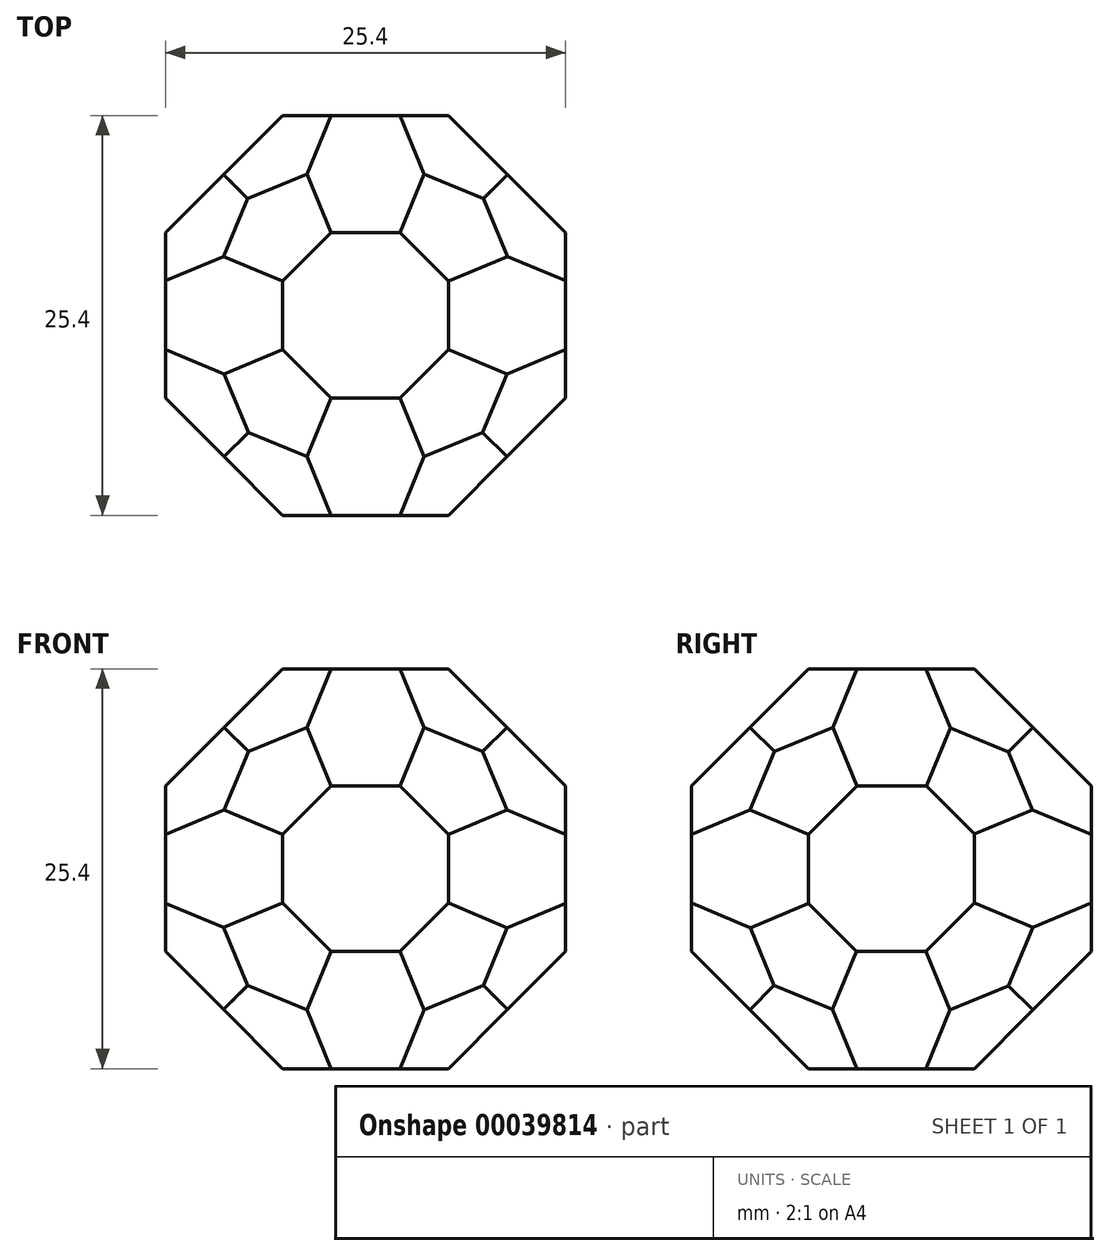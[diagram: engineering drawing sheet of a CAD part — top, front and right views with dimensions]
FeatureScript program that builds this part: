
annotation { "Feature Type Name" : "Feature", "Feature Type Description" : "" }
export const myFeature = defineFeature(function(context is Context, id is Id, definition is map)
    precondition{}
    {
        {
            var Q0;
            Q0=qCreatedBy(makeId("Right.planeOp"),FACE);
            var sketch = newSketch(context, id + "F0", { "sketchPlane" : qUnion([Q0])});
            skCircle(sketch, "E0.cCircle", {"center": v(0, 0) * mm, "radius": 12.7 * mm, "construction": true});
            skLineSegment(sketch, "E0.0", {"start": v(-5.26, 12.7) * mm, "end": v(5.26, 12.7) * mm});
            skLineSegment(sketch, "E0.1", {"start": v(5.26, 12.7) * mm, "end": v(12.7, 5.26) * mm});
            skLineSegment(sketch, "E0.2", {"start": v(12.7, 5.26) * mm, "end": v(12.7, -5.26) * mm});
            skLineSegment(sketch, "E0.3", {"start": v(12.7, -5.26) * mm, "end": v(5.26, -12.7) * mm});
            skLineSegment(sketch, "E0.4", {"start": v(5.26, -12.7) * mm, "end": v(-5.26, -12.7) * mm});
            skLineSegment(sketch, "E0.5", {"start": v(-5.26, -12.7) * mm, "end": v(-12.7, -5.26) * mm});
            skLineSegment(sketch, "E0.6", {"start": v(-12.7, -5.26) * mm, "end": v(-12.7, 5.26) * mm});
            skLineSegment(sketch, "E0.7", {"start": v(-12.7, 5.26) * mm, "end": v(-5.26, 12.7) * mm});
            skPoint(sketch, "E0.0.midPoint", {"position": v(0, 12.7) * mm});
            skSolve(sketch);
        }
        {
            var Q0;
            Q0 = qSketchRegion(id + "F0", true);
            extrude(context, id + "F1", {"entities" : qUnion([Q0]), "endBound" : BoundingType.SYMMETRIC, "depth" : 25.4 * mm});
        }
        {
            var Q0;
            Q0=qCreatedBy(makeId("Top.planeOp"),FACE);
            var sketch = newSketch(context, id + "F2", { "sketchPlane" : qUnion([Q0])});
            skArc(sketch, "E1.cCircle", {"start": v(-8.98, 8.98) * mm, "mid": v(4.86, -11.73) * mm, "end": v(0, 12.7) * mm, "construction": true});
            skLineSegment(sketch, "E1.1", {"start": v(5.26, 12.7) * mm, "end": v(12.7, 5.26) * mm});
            skLineSegment(sketch, "E1.3", {"start": v(12.7, -5.26) * mm, "end": v(5.26, -12.7) * mm});
            skLineSegment(sketch, "E1.5", {"start": v(-5.26, -12.7) * mm, "end": v(-12.7, -5.26) * mm});
            skLineSegment(sketch, "E1.7", {"start": v(-12.7, 5.26) * mm, "end": v(-5.26, 12.7) * mm});
            skPoint(sketch, "E1.0.midPoint", {"position": v(0, 12.7) * mm});
            skLineSegment(sketch, "E2", {"start": v(-12.7, 5.26) * mm, "end": v(-12.7, 13.88) * mm});
            skLineSegment(sketch, "E3", {"start": v(-12.7, 13.88) * mm, "end": v(-12.7, 12.75) * mm});
            skLineSegment(sketch, "E4", {"start": v(-5.26, 12.7) * mm, "end": v(-13.31, 12.75) * mm});
            skLineSegment(sketch, "E5", {"start": v(-13.31, 12.75) * mm, "end": v(-12.7, 12.75) * mm});
            skLineSegment(sketch, "E6", {"start": v(16.73, 12.75) * mm, "end": v(12.98, 12.75) * mm});
            skLineSegment(sketch, "E7", {"start": v(12.7, 5.26) * mm, "end": v(12.7, 12.75) * mm});
            skLineSegment(sketch, "E8", {"start": v(12.7, 12.75) * mm, "end": v(12.7, 5.26) * mm});
            skLineSegment(sketch, "E9", {"start": v(12.7, 5.26) * mm, "end": v(5.26, 12.7) * mm});
            skLineSegment(sketch, "E10.0", {"start": v(12.7, -12.7) * mm, "end": v(12.7, -5.26) * mm});
            skLineSegment(sketch, "E11.0", {"start": v(12.7, -12.7) * mm, "end": v(-12.7, -12.7) * mm});
            skLineSegment(sketch, "E12.0", {"start": v(-12.7, -12.7) * mm, "end": v(-12.7, -5.26) * mm});
            skLineSegment(sketch, "E13.trimOffspring", {"start": v(12.7, 12.75) * mm, "end": v(16.73, 12.75) * mm});
            skLineSegment(sketch, "E14", {"start": v(5.26, 12.7) * mm, "end": v(14.71, 12.75) * mm});
            skSolve(sketch);
        }
        {
            var Q0;
            Q0 = qSketchRegion(id + "F2", true);
            extrude(context, id + "F3", {"entities" : qUnion([Q0]), "operationType" : NewBodyOperationType.REMOVE, "endBound" : BoundingType.SYMMETRIC, "oppositeDirection" : true, "depth" : 25.4 * mm});
        }
        {
            var Q0;
            Q0=makeQuery(id+"F1.opExtrude","SWEPT_FACE",FACE,{"disambiguationData":[OSD([sQuery(id+"F0.wireOp",EDGE,"E0.2")])]});
            var sketch = newSketch(context, id + "F4", { "sketchPlane" : qUnion([Q0])});
            skArc(sketch, "E15.cCircle", {"start": v(-8.98, 8.98) * mm, "mid": v(-8.98, -8.98) * mm, "end": v(8.98, -8.98) * mm, "construction": true});
            skLineSegment(sketch, "E15.1", {"start": v(5.26, 12.7) * mm, "end": v(12.7, 5.26) * mm});
            skLineSegment(sketch, "E15.3", {"start": v(12.7, -5.26) * mm, "end": v(5.26, -12.7) * mm});
            skLineSegment(sketch, "E15.4", {"start": v(5.26, -12.7) * mm, "end": v(-5.26, -12.7) * mm});
            skLineSegment(sketch, "E15.5", {"start": v(-5.26, -12.7) * mm, "end": v(-12.7, -5.26) * mm});
            skLineSegment(sketch, "E15.6", {"start": v(-12.7, -5.26) * mm, "end": v(-12.7, 0) * mm});
            skLineSegment(sketch, "E15.7", {"start": v(-12.7, 5.26) * mm, "end": v(-5.26, 12.7) * mm});
            skPoint(sketch, "E15.0.midPoint", {"position": v(0, 12.7) * mm});
            skPoint(sketch, "E16.0.start.orphan", {"position": v(-12.7, 12.7) * mm});
            skPoint(sketch, "E17.0.end.orphan", {"position": v(12.7, 12.7) * mm});
            skPoint(sketch, "E18.0.end.orphan", {"position": v(12.7, -12.7) * mm});
            skPoint(sketch, "E18.0.start.orphan", {"position": v(-12.7, -12.7) * mm});
            skLineSegment(sketch, "E19.0", {"start": v(-12.7, -12.7) * mm, "end": v(-12.7, -5.26) * mm});
            skLineSegment(sketch, "E20.0", {"start": v(-12.7, 12.7) * mm, "end": v(-5.26, 12.7) * mm});
            skLineSegment(sketch, "E21.0", {"start": v(12.7, -12.7) * mm, "end": v(12.7, -5.26) * mm});
            skLineSegment(sketch, "E22.0", {"start": v(-12.7, -12.7) * mm, "end": v(0, -12.7) * mm});
            skLineSegment(sketch, "E23.trimOffspring", {"start": v(-12.7, 5.26) * mm, "end": v(-12.7, 12.7) * mm});
            skLineSegment(sketch, "E24.trimOffspring", {"start": v(5.26, 12.7) * mm, "end": v(12.7, 12.7) * mm});
            skLineSegment(sketch, "E25.trimOffspring", {"start": v(12.7, 0) * mm, "end": v(12.7, 12.7) * mm});
            skLineSegment(sketch, "E26.trimOffspring", {"start": v(5.26, -12.7) * mm, "end": v(12.7, -12.7) * mm});
            skSolve(sketch);
        }
        {
            var Q0;
            Q0 = qSketchRegion(id + "F4", true);
            extrude(context, id + "F5", {"entities" : qUnion([Q0]), "operationType" : NewBodyOperationType.REMOVE, "oppositeDirection" : true, "depth" : 25.4 * mm});
        }
        {
            var Q0;
            Q0=makeQuery(id+"F1.opExtrude","SWEPT_FACE",FACE,{"disambiguationData":[OSD([sQuery(id+"F0.wireOp",EDGE,"E0.7")])]});
            var sketch = newSketch(context, id + "F6", { "sketchPlane" : qUnion([Q0])});
            skCircle(sketch, "E27.cCircle", {"center": v(0, 0) * mm, "radius": 12.72 * mm, "construction": true});
            skLineSegment(sketch, "E27.0", {"start": v(-12.72, -5.27) * mm, "end": v(-12.72, 5.27) * mm});
            skLineSegment(sketch, "E27.1", {"start": v(-12.72, 5.27) * mm, "end": v(-5.27, 12.72) * mm});
            skLineSegment(sketch, "E27.2", {"start": v(-5.27, 12.72) * mm, "end": v(5.27, 12.72) * mm});
            skLineSegment(sketch, "E27.3", {"start": v(5.27, 12.72) * mm, "end": v(12.72, 5.27) * mm});
            skLineSegment(sketch, "E27.4", {"start": v(12.72, 0) * mm, "end": v(12.72, -5.27) * mm});
            skLineSegment(sketch, "E27.5", {"start": v(12.72, -5.27) * mm, "end": v(5.27, -12.72) * mm});
            skLineSegment(sketch, "E27.6", {"start": v(5.27, -12.72) * mm, "end": v(0, -12.72) * mm});
            skLineSegment(sketch, "E27.7", {"start": v(-5.27, -12.72) * mm, "end": v(-12.72, -5.27) * mm});
            skPoint(sketch, "E27.0.midPoint", {"position": v(-12.72, 0) * mm});
            skLineSegment(sketch, "E28", {"start": v(-5.27, -12.72) * mm, "end": v(-14.84, -12.72) * mm});
            skLineSegment(sketch, "E29", {"start": v(-14.84, -12.72) * mm, "end": v(-14.84, -4.68) * mm});
            skLineSegment(sketch, "E30", {"start": v(-14.84, -4.68) * mm, "end": v(-12.72, -5.27) * mm});
            skLineSegment(sketch, "E31", {"start": v(-12.72, 5.27) * mm, "end": v(-16.15, 5.27) * mm});
            skLineSegment(sketch, "E32", {"start": v(-16.15, 5.27) * mm, "end": v(-10.66, 15.36) * mm});
            skLineSegment(sketch, "E33", {"start": v(-10.66, 15.36) * mm, "end": v(-5.27, 12.72) * mm});
            skLineSegment(sketch, "E34", {"start": v(5.27, 12.72) * mm, "end": v(11.88, 14.74) * mm});
            skLineSegment(sketch, "E35", {"start": v(11.88, 14.74) * mm, "end": v(15.12, 7.12) * mm});
            skLineSegment(sketch, "E36", {"start": v(15.12, 7.12) * mm, "end": v(12.72, 5.27) * mm});
            skLineSegment(sketch, "E37", {"start": v(5.27, -12.72) * mm, "end": v(11.63, -17.16) * mm});
            skLineSegment(sketch, "E38", {"start": v(11.63, -17.16) * mm, "end": v(17.18, -6.74) * mm});
            skLineSegment(sketch, "E39", {"start": v(17.18, -6.74) * mm, "end": v(12.72, -5.27) * mm});
            skSolve(sketch);
        }
        {
            var Q0;
            Q0 = qSketchRegion(id + "F6", true);
            extrude(context, id + "F7", {"entities" : qUnion([Q0]), "operationType" : NewBodyOperationType.REMOVE, "oppositeDirection" : true, "depth" : 25.4 * mm});
        }
        {
            var Q0;
            Q0=makeQuery(id+"F1.opExtrude","SWEPT_FACE",FACE,{"disambiguationData":[OSD([sQuery(id+"F0.wireOp",EDGE,"E0.5")])]});
            var sketch = newSketch(context, id + "F8", { "sketchPlane" : qUnion([Q0])});
            skCircle(sketch, "E40.cCircle", {"center": v(0, 0) * mm, "radius": 12.7 * mm, "construction": true});
            skLineSegment(sketch, "E40.0", {"start": v(12.7, 5.26) * mm, "end": v(12.7, -5.26) * mm});
            skLineSegment(sketch, "E40.1", {"start": v(12.7, -5.26) * mm, "end": v(5.26, -12.7) * mm});
            skLineSegment(sketch, "E40.2", {"start": v(5.26, -12.7) * mm, "end": v(-5.26, -12.7) * mm});
            skLineSegment(sketch, "E40.3", {"start": v(-5.26, -12.7) * mm, "end": v(-12.7, -5.26) * mm});
            skLineSegment(sketch, "E40.4", {"start": v(-12.7, -5.26) * mm, "end": v(-12.7, 5.26) * mm});
            skLineSegment(sketch, "E40.5", {"start": v(-12.7, 5.26) * mm, "end": v(-5.26, 12.7) * mm});
            skLineSegment(sketch, "E40.6", {"start": v(-5.26, 12.7) * mm, "end": v(5.26, 12.7) * mm});
            skLineSegment(sketch, "E40.7", {"start": v(5.26, 12.7) * mm, "end": v(12.7, 5.26) * mm});
            skPoint(sketch, "E40.0.midPoint", {"position": v(12.7, 0) * mm});
            skLineSegment(sketch, "E41", {"start": v(12.7, 5.26) * mm, "end": v(15.02, 5.97) * mm});
            skLineSegment(sketch, "E42", {"start": v(15.02, 5.97) * mm, "end": v(8.38, 16.37) * mm});
            skLineSegment(sketch, "E43", {"start": v(8.38, 16.37) * mm, "end": v(5.26, 12.7) * mm});
            skLineSegment(sketch, "E44", {"start": v(-5.26, 12.7) * mm, "end": v(-10.87, 17.6) * mm});
            skLineSegment(sketch, "E45", {"start": v(-10.87, 17.6) * mm, "end": v(-15.85, 5.64) * mm});
            skLineSegment(sketch, "E46", {"start": v(-15.85, 5.64) * mm, "end": v(-12.7, 5.26) * mm});
            skLineSegment(sketch, "E47", {"start": v(-12.7, -5.26) * mm, "end": v(-15.77, -8.33) * mm});
            skLineSegment(sketch, "E48", {"start": v(-15.77, -8.33) * mm, "end": v(-6.61, -16.65) * mm});
            skLineSegment(sketch, "E49", {"start": v(-6.61, -16.65) * mm, "end": v(-5.26, -12.7) * mm});
            skLineSegment(sketch, "E50", {"start": v(12.7, -5.26) * mm, "end": v(16.3, -8.85) * mm});
            skLineSegment(sketch, "E51", {"start": v(16.3, -8.85) * mm, "end": v(9.21, -16.87) * mm});
            skLineSegment(sketch, "E52", {"start": v(9.21, -16.87) * mm, "end": v(5.26, -12.7) * mm});
            skSolve(sketch);
        }
        {
            var Q0;
            Q0=makeQuery(id+"F8.imprint","IMPRINT",FACE,{"disambiguationData":[TD([[makeQuery(id+"F8.imprint","IMPRINT",EDGE,{"derivedFrom":sQuery(id+"F8.wireOp",EDGE,"E40.1")}),1.0]])]});
            var Q1;
            Q1=makeQuery(id+"F8.imprint","IMPRINT",FACE,{"disambiguationData":[TD([[makeQuery(id+"F8.imprint","IMPRINT",EDGE,{"derivedFrom":sQuery(id+"F8.wireOp",EDGE,"E40.3")}),1.0]])]});
            var Q2;
            Q2=makeQuery(id+"F8.imprint","IMPRINT",FACE,{"disambiguationData":[TD([[makeQuery(id+"F8.imprint","IMPRINT",EDGE,{"derivedFrom":sQuery(id+"F8.wireOp",EDGE,"E40.5")}),1.0]])]});
            var Q3;
            Q3=makeQuery(id+"F8.imprint","IMPRINT",FACE,{"disambiguationData":[TD([[makeQuery(id+"F8.imprint","IMPRINT",EDGE,{"derivedFrom":sQuery(id+"F8.wireOp",EDGE,"E40.7")}),1.0]])]});
            extrude(context, id + "F9", {"entities" : qUnion([Q0, Q1, Q2, Q3]), "operationType" : NewBodyOperationType.REMOVE, "oppositeDirection" : true, "depth" : 25.4 * mm});
        }
        {
            var Q0;
            Q0=makeQuery(id+"F5.boolean.opBoolean","COPY",FACE,{"derivedFrom":makeQuery(id+"F5.opExtrude","SWEPT_FACE",FACE,{"disambiguationData":[OSD([sQuery(id+"F4.wireOp",EDGE,"E15.1")])]})});
            var sketch = newSketch(context, id + "F10", { "sketchPlane" : qUnion([Q0])});
            skCircle(sketch, "E53.cCircle", {"center": v(0, 0) * mm, "radius": 12.7 * mm, "construction": true});
            skLineSegment(sketch, "E53.0", {"start": v(0, 12.7) * mm, "end": v(5.26, 12.7) * mm});
            skLineSegment(sketch, "E53.1", {"start": v(5.26, 12.7) * mm, "end": v(12.7, 5.26) * mm});
            skLineSegment(sketch, "E53.2", {"start": v(12.7, 5.26) * mm, "end": v(12.7, -5.26) * mm});
            skLineSegment(sketch, "E53.3", {"start": v(12.7, -5.26) * mm, "end": v(5.26, -12.7) * mm});
            skLineSegment(sketch, "E53.4", {"start": v(5.26, -12.7) * mm, "end": v(-5.26, -12.7) * mm});
            skLineSegment(sketch, "E53.5", {"start": v(-5.26, -12.7) * mm, "end": v(-12.7, -5.26) * mm});
            skLineSegment(sketch, "E53.6", {"start": v(-12.7, -5.26) * mm, "end": v(-12.7, 5.26) * mm});
            skLineSegment(sketch, "E53.7", {"start": v(-12.7, 5.26) * mm, "end": v(-5.26, 12.7) * mm});
            skPoint(sketch, "E53.0.midPoint", {"position": v(0, 12.7) * mm});
            skLineSegment(sketch, "E54", {"start": v(-12.7, 5.26) * mm, "end": v(-12.7, 11.55) * mm});
            skLineSegment(sketch, "E55", {"start": v(-12.7, 11.55) * mm, "end": v(-5.26, 12.7) * mm});
            skLineSegment(sketch, "E56", {"start": v(5.26, 12.7) * mm, "end": v(15.02, 11.13) * mm});
            skLineSegment(sketch, "E57", {"start": v(15.02, 11.13) * mm, "end": v(12.7, 5.26) * mm});
            skLineSegment(sketch, "E58", {"start": v(12.7, -5.26) * mm, "end": v(14.34, -10.45) * mm});
            skLineSegment(sketch, "E59", {"start": v(14.34, -10.45) * mm, "end": v(5.26, -12.7) * mm});
            skLineSegment(sketch, "E60", {"start": v(-5.26, -12.7) * mm, "end": v(-13.06, -10.45) * mm});
            skLineSegment(sketch, "E61", {"start": v(-13.06, -10.45) * mm, "end": v(-12.7, -5.26) * mm});
            skSolve(sketch);
        }
        {
            var Q0;
            Q0 = qSketchRegion(id + "F10", true);
            extrude(context, id + "F11", {"entities" : qUnion([Q0]), "operationType" : NewBodyOperationType.REMOVE, "oppositeDirection" : true, "depth" : 25.4 * mm});
        }
        {
            var Q0;
            Q0=makeQuery(id+"F3.boolean.opBoolean","COPY",FACE,{"derivedFrom":makeQuery(id+"F3.opExtrude","SWEPT_FACE",FACE,{"disambiguationData":[OSD([sQuery(id+"F2.wireOp",EDGE,"E1.7")])]})});
            var sketch = newSketch(context, id + "F12", { "sketchPlane" : qUnion([Q0])});
            skCircle(sketch, "E62.cCircle", {"center": v(0, 0) * mm, "radius": 12.7 * mm, "construction": true});
            skLineSegment(sketch, "E62.0", {"start": v(12.7, 0) * mm, "end": v(12.7, -5.26) * mm});
            skLineSegment(sketch, "E62.1", {"start": v(12.7, -5.26) * mm, "end": v(5.26, -12.7) * mm});
            skLineSegment(sketch, "E62.2", {"start": v(5.26, -12.7) * mm, "end": v(-5.26, -12.7) * mm});
            skLineSegment(sketch, "E62.3", {"start": v(-5.26, -12.7) * mm, "end": v(-12.7, -5.26) * mm});
            skLineSegment(sketch, "E62.4", {"start": v(-12.7, -5.26) * mm, "end": v(-12.7, 5.26) * mm});
            skLineSegment(sketch, "E62.5", {"start": v(-12.7, 5.26) * mm, "end": v(-5.26, 12.7) * mm});
            skLineSegment(sketch, "E62.6", {"start": v(-5.26, 12.7) * mm, "end": v(5.26, 12.7) * mm});
            skLineSegment(sketch, "E62.7", {"start": v(5.26, 12.7) * mm, "end": v(12.7, 5.26) * mm});
            skPoint(sketch, "E62.0.midPoint", {"position": v(12.7, 0) * mm});
            skLineSegment(sketch, "E63.0", {"start": v(7.44, 12.7) * mm, "end": v(0, 12.7) * mm});
            skLineSegment(sketch, "E64.0", {"start": v(7.44, 12.7) * mm, "end": v(12.7, 5.26) * mm});
            skLineSegment(sketch, "E65.0", {"start": v(-12.7, 3.74) * mm, "end": v(-7.5, 12.62) * mm});
            skLineSegment(sketch, "E66.0", {"start": v(-12.7, -5.26) * mm, "end": v(-7.44, -12.7) * mm});
            skLineSegment(sketch, "E67.0", {"start": v(7.5, -12.62) * mm, "end": v(12.7, -3.74) * mm});
            skLineSegment(sketch, "E68.0", {"start": v(7.44, -12.7) * mm, "end": v(0, -12.7) * mm});
            skLineSegment(sketch, "E69.0", {"start": v(-7.44, 12.7) * mm, "end": v(0, 12.7) * mm});
            skLineSegment(sketch, "E70.0", {"start": v(-7.44, -12.7) * mm, "end": v(0, -12.7) * mm});
            skLineSegment(sketch, "E71", {"start": v(-7.44, 12.7) * mm, "end": v(-14.2, 11.6) * mm});
            skLineSegment(sketch, "E72", {"start": v(-14.2, 11.6) * mm, "end": v(-12.67, 5.52) * mm});
            skLineSegment(sketch, "E73", {"start": v(-12.67, 5.52) * mm, "end": v(-12.7, 5.26) * mm});
            skLineSegment(sketch, "E74", {"start": v(7.44, 12.7) * mm, "end": v(16.3, 11.82) * mm});
            skLineSegment(sketch, "E75", {"start": v(16.3, 11.82) * mm, "end": v(12.7, 5.26) * mm});
            skLineSegment(sketch, "E76", {"start": v(12.7, -5.26) * mm, "end": v(16.97, -14.22) * mm});
            skLineSegment(sketch, "E77", {"start": v(16.97, -14.22) * mm, "end": v(7.44, -12.7) * mm});
            skLineSegment(sketch, "E78", {"start": v(-12.7, -5.26) * mm, "end": v(-17.62, -12.86) * mm});
            skLineSegment(sketch, "E79", {"start": v(-17.62, -12.86) * mm, "end": v(-7.44, -12.7) * mm});
            skSolve(sketch);
        }
        {
            var Q0;
            Q0 = qSketchRegion(id + "F12", true);
            extrude(context, id + "F13", {"entities" : qUnion([Q0]), "operationType" : NewBodyOperationType.REMOVE, "oppositeDirection" : true, "depth" : 25.4 * mm});
        }
        {
            var Q0;
            {var subQ0=sQuery(id+"F0.wireOp",EDGE,"E0.3");Q0=makeQuery(id+"F11.boolean.opBoolean","SPLIT",FACE,{"disambiguationData":[TD([makeQuery(id+"F1.opExtrude","SWEPT_FACE",FACE,{"disambiguationData":[OSD([subQ0])]})])],"derivedFrom":makeQuery(id+"F5.boolean.opBoolean","COPY",FACE,{"derivedFrom":makeQuery(id+"F5.opExtrude","SWEPT_FACE",FACE,{"disambiguationData":[OSD([sQuery(id+"F4.wireOp",EDGE,"E15.3")])]})})});}
            var sketch = newSketch(context, id + "F14", { "sketchPlane" : qUnion([Q0])});
            skCircle(sketch, "E80.cCircle", {"center": v(0, 0) * mm, "radius": 12.7 * mm, "construction": true});
            skLineSegment(sketch, "E80.0", {"start": v(0, 12.7) * mm, "end": v(5.26, 12.7) * mm});
            skLineSegment(sketch, "E80.1", {"start": v(5.26, 12.7) * mm, "end": v(12.7, 5.26) * mm});
            skLineSegment(sketch, "E80.2", {"start": v(12.7, 5.26) * mm, "end": v(12.7, -5.26) * mm});
            skLineSegment(sketch, "E80.3", {"start": v(12.7, -5.26) * mm, "end": v(5.26, -12.7) * mm});
            skLineSegment(sketch, "E80.4", {"start": v(5.26, -12.7) * mm, "end": v(-5.26, -12.7) * mm});
            skLineSegment(sketch, "E80.5", {"start": v(-5.26, -12.7) * mm, "end": v(-12.7, -5.26) * mm});
            skLineSegment(sketch, "E80.6", {"start": v(-12.7, -5.26) * mm, "end": v(-12.7, 5.26) * mm});
            skLineSegment(sketch, "E80.7", {"start": v(-12.7, 5.26) * mm, "end": v(-5.26, 12.7) * mm});
            skPoint(sketch, "E80.0.midPoint", {"position": v(0, 12.7) * mm});
            skLineSegment(sketch, "E81.0", {"start": v(-12.7, 2.18) * mm, "end": v(-12.7, 7.44) * mm});
            skLineSegment(sketch, "E82.0", {"start": v(-5.28, 12.7) * mm, "end": v(-12.68, 7.47) * mm});
            skLineSegment(sketch, "E83.0", {"start": v(12.7, 7.44) * mm, "end": v(3.72, 12.7) * mm});
            skLineSegment(sketch, "E84.0", {"start": v(12.7, 2.18) * mm, "end": v(12.7, 7.44) * mm});
            skLineSegment(sketch, "E85.0", {"start": v(12.7, -7.44) * mm, "end": v(12.7, -2.18) * mm});
            skLineSegment(sketch, "E86.0", {"start": v(-12.7, -7.44) * mm, "end": v(-12.7, -2.18) * mm});
            skLineSegment(sketch, "E87.0", {"start": v(-3.72, -12.7) * mm, "end": v(-12.7, -7.44) * mm});
            skLineSegment(sketch, "E88", {"start": v(-5.26, 12.7) * mm, "end": v(0, 12.7) * mm});
            skLineSegment(sketch, "E89", {"start": v(-12.7, 5.26) * mm, "end": v(-16.48, 10.8) * mm});
            skLineSegment(sketch, "E90", {"start": v(-16.48, 10.8) * mm, "end": v(-5.26, 12.7) * mm});
            skLineSegment(sketch, "E91", {"start": v(12.7, 7.44) * mm, "end": v(5.26, 12.7) * mm});
            skLineSegment(sketch, "E92", {"start": v(12.7, -7.44) * mm, "end": v(13.68, -12.16) * mm});
            skLineSegment(sketch, "E93", {"start": v(13.68, -12.16) * mm, "end": v(5.28, -12.7) * mm});
            skLineSegment(sketch, "E94", {"start": v(-5.26, -12.7) * mm, "end": v(-10.99, -13.6) * mm});
            skLineSegment(sketch, "E95", {"start": v(-10.99, -13.6) * mm, "end": v(-12.7, -7.44) * mm});
            skLineSegment(sketch, "E96", {"start": v(5.28, -12.7) * mm, "end": v(12.7, -5.26) * mm});
            skPoint(sketch, "E97.0.start.orphan", {"position": v(12.68, -7.47) * mm});
            skSolve(sketch);
        }
        {
            var Q0;
            {var subQ2=sQuery(id+"F14.wireOp",EDGE,"E80.7");Q0=makeQuery(id+"F14.imprint","IMPRINT",FACE,{"disambiguationData":[TD([[makeQuery(id+"F14.imprint","IMPRINT",EDGE,{"derivedFrom":subQ2}),1.0]])]});}
            var Q1;
            {var subQ0=sQuery(id+"F14.wireOp",EDGE,"E83.0");var subQ3=sQuery(id+"F14.wireOp",EDGE,"E80.0");var subQ4=makeQuery(id+"F14.imprint","INTERSECT",VERTEX,{"derivedFrom":[subQ3,subQ0]});Q1=makeQuery(id+"F14.imprint","IMPRINT",FACE,{"disambiguationData":[TD([[makeQuery(id+"F14.imprint","IMPRINT",EDGE,{"disambiguationData":[TD([[subQ4,1.0]])],"derivedFrom":subQ0}),-1.0]])]});}
            var Q2;
            {var subQ0=sQuery(id+"F14.wireOp",EDGE,"E91");Q2=makeQuery(id+"F14.imprint","IMPRINT",FACE,{"disambiguationData":[TD([[makeQuery(id+"F14.imprint","IMPRINT",EDGE,{"derivedFrom":subQ0}),1.0]])]});}
            var Q3;
            {var subQ0=sQuery(id+"F14.wireOp",EDGE,"E84.0");var subQ3=sQuery(id+"F14.wireOp",EDGE,"E80.1");var subQ4=makeQuery(id+"F14.imprint","INTERSECT",VERTEX,{"derivedFrom":[subQ3,subQ0]});Q3=makeQuery(id+"F14.imprint","IMPRINT",FACE,{"disambiguationData":[TD([[makeQuery(id+"F14.imprint","IMPRINT",EDGE,{"disambiguationData":[TD([[subQ4,1.0]])],"derivedFrom":subQ3}),1.0]])]});}
            var Q4;
            {var subQ0=sQuery(id+"F14.wireOp",EDGE,"E87.0");var subQ3=sQuery(id+"F14.wireOp",EDGE,"E80.4");var subQ4=makeQuery(id+"F14.imprint","INTERSECT",VERTEX,{"derivedFrom":[subQ3,subQ0]});Q4=makeQuery(id+"F14.imprint","IMPRINT",FACE,{"disambiguationData":[TD([[makeQuery(id+"F14.imprint","IMPRINT",EDGE,{"disambiguationData":[TD([[subQ4,-1.0]])],"derivedFrom":subQ0}),1.0]])]});}
            var Q5;
            {var subQ0=sQuery(id+"F14.wireOp",EDGE,"E94");Q5=makeQuery(id+"F14.imprint","IMPRINT",FACE,{"disambiguationData":[TD([[makeQuery(id+"F14.imprint","IMPRINT",EDGE,{"derivedFrom":subQ0}),-1.0]])]});}
            var Q6;
            {var subQ1=sQuery(id+"F14.wireOp",EDGE,"E80.5");var subQ3=sQuery(id+"F14.wireOp",EDGE,"E86.0");var subQ5=makeQuery(id+"F14.imprint","INTERSECT",VERTEX,{"derivedFrom":[subQ1,subQ3]});Q6=makeQuery(id+"F14.imprint","IMPRINT",FACE,{"disambiguationData":[TD([[makeQuery(id+"F14.imprint","IMPRINT",EDGE,{"disambiguationData":[TD([[subQ5,1.0]])],"derivedFrom":subQ1}),1.0]])]});}
            var Q7;
            {var subQ1=sQuery(id+"F14.wireOp",EDGE,"E92");Q7=makeQuery(id+"F14.imprint","IMPRINT",FACE,{"disambiguationData":[TD([[makeQuery(id+"F14.imprint","IMPRINT",EDGE,{"derivedFrom":subQ1}),-1.0]])]});}
            extrude(context, id + "F15", {"entities" : qUnion([Q0, Q1, Q2, Q3, Q4, Q5, Q6, Q7]), "operationType" : NewBodyOperationType.REMOVE, "oppositeDirection" : true, "depth" : 25.4 * mm});
        }
        {
            var Q0;
            Q0=makeQuery(id+"F3.boolean.opBoolean","COPY",FACE,{"derivedFrom":makeQuery(id+"F3.opExtrude","SWEPT_FACE",FACE,{"disambiguationData":[OSD([sQuery(id+"F2.wireOp",EDGE,"E1.5")])]})});
            var sketch = newSketch(context, id + "F16", { "sketchPlane" : qUnion([Q0])});
            skCircle(sketch, "E98.cCircle", {"center": v(0, 0) * mm, "radius": 12.7 * mm, "construction": true});
            skLineSegment(sketch, "E98.0", {"start": v(-12.7, 0) * mm, "end": v(-12.7, 5.26) * mm});
            skLineSegment(sketch, "E98.1", {"start": v(-12.7, 5.26) * mm, "end": v(-5.26, 12.7) * mm});
            skLineSegment(sketch, "E98.2", {"start": v(-5.26, 12.7) * mm, "end": v(5.26, 12.7) * mm});
            skLineSegment(sketch, "E98.3", {"start": v(5.26, 12.7) * mm, "end": v(12.7, 5.26) * mm});
            skLineSegment(sketch, "E98.4", {"start": v(12.7, 5.26) * mm, "end": v(12.7, -5.26) * mm});
            skLineSegment(sketch, "E98.5", {"start": v(12.7, -5.26) * mm, "end": v(5.26, -12.7) * mm});
            skLineSegment(sketch, "E98.6", {"start": v(5.26, -12.7) * mm, "end": v(-5.26, -12.7) * mm});
            skLineSegment(sketch, "E98.7", {"start": v(-5.26, -12.7) * mm, "end": v(-12.7, -5.26) * mm});
            skPoint(sketch, "E98.0.midPoint", {"position": v(-12.7, 0) * mm});
            skLineSegment(sketch, "E99", {"start": v(-5.26, -12.7) * mm, "end": v(-11.03, -16.38) * mm});
            skLineSegment(sketch, "E100", {"start": v(-11.03, -16.38) * mm, "end": v(-12.7, -5.26) * mm});
            skLineSegment(sketch, "E101", {"start": v(-12.7, 5.26) * mm, "end": v(-9.48, 22.07) * mm});
            skLineSegment(sketch, "E102", {"start": v(-9.48, 22.07) * mm, "end": v(-5.26, 12.7) * mm});
            skLineSegment(sketch, "E103", {"start": v(5.26, 12.7) * mm, "end": v(10.58, 18.02) * mm});
            skLineSegment(sketch, "E104", {"start": v(10.58, 18.02) * mm, "end": v(12.7, 5.26) * mm});
            skLineSegment(sketch, "E105", {"start": v(12.7, -5.26) * mm, "end": v(13.76, -15.2) * mm});
            skLineSegment(sketch, "E106", {"start": v(13.76, -15.2) * mm, "end": v(5.26, -12.7) * mm});
            skSolve(sketch);
        }
        {
            var Q0;
            Q0 = qSketchRegion(id + "F16", true);
            extrude(context, id + "F17", {"entities" : qUnion([Q0]), "operationType" : NewBodyOperationType.REMOVE, "oppositeDirection" : true, "depth" : 25.4 * mm});
        }
    });
